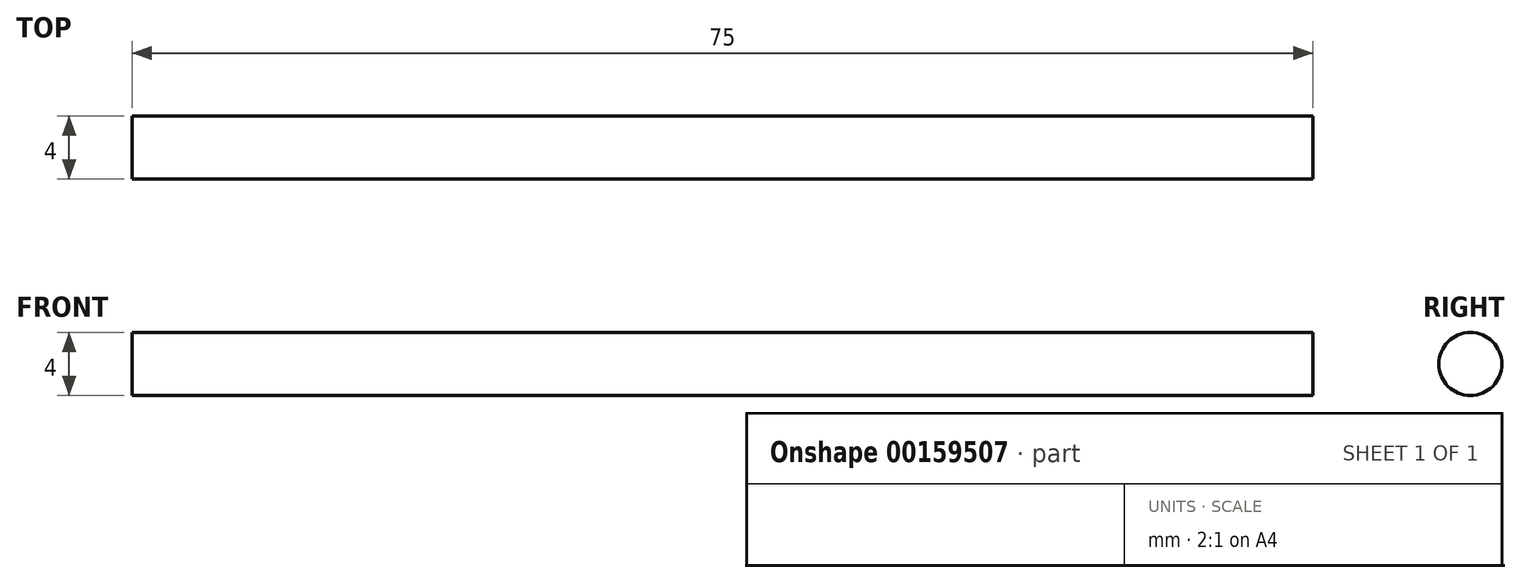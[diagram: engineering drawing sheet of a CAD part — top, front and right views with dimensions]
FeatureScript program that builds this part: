
annotation { "Feature Type Name" : "Feature", "Feature Type Description" : "" }
export const myFeature = defineFeature(function(context is Context, id is Id, definition is map)
    precondition{}
    {
        {
            var Q0;
            Q0=qCreatedBy(makeId("Right.planeOp"),FACE);
            var sketch = newSketch(context, id + "F0", { "sketchPlane" : qUnion([Q0])});
            skCircle(sketch, "E0", {"center": v(0, 0) * mm, "radius": 2 * mm});
            skSolve(sketch);
        }
        {
            var Q0;
            Q0 = qSketchRegion(id + "F0", true);
            extrude(context, id + "F1", {"entities" : qUnion([Q0]), "depth" : 75 * mm});
        }
    });
